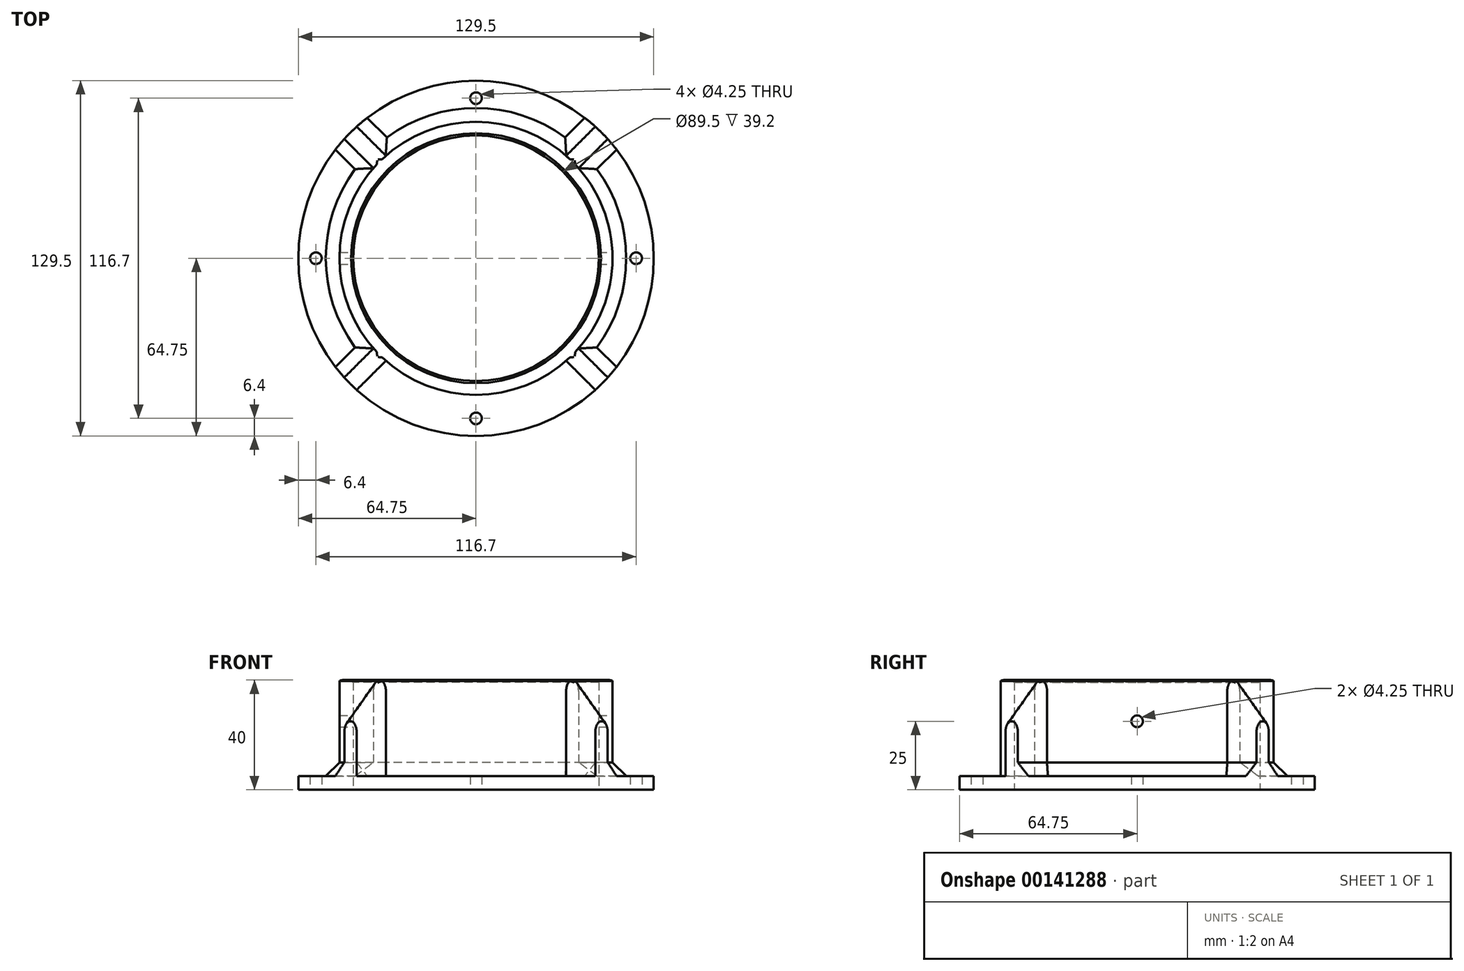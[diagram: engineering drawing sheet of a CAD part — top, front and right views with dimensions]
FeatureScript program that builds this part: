
annotation { "Feature Type Name" : "Feature", "Feature Type Description" : "" }
export const myFeature = defineFeature(function(context is Context, id is Id, definition is map)
    precondition{}
    {
        {
            var Q0;
            Q0=qCreatedBy(makeId("Top.planeOp"),FACE);
            var sketch = newSketch(context, id + "F0", { "sketchPlane" : qUnion([Q0])});
            skCircle(sketch, "E0", {"center": v(0, 0) * mm, "radius": 44.75 * mm});
            skCircle(sketch, "E1", {"center": v(0, 0) * mm, "radius": 64.75 * mm});
            skCircle(sketch, "E2", {"center": v(58.35, 0) * mm, "radius": 2.12 * mm});
            skCircle(sketch, "E3.1.0", {"center": v(0, 58.35) * mm, "radius": 2.12 * mm});
            skCircle(sketch, "E3.2.0", {"center": v(-58.35, 0) * mm, "radius": 2.12 * mm});
            skCircle(sketch, "E3.3.0", {"center": v(0, -58.35) * mm, "radius": 2.12 * mm});
            skSolve(sketch);
        }
        {
            var Q0;
            Q0=qSketchRegion(id+"F0",true);
            extrude(context, id + "F1", {"entities" : qUnion([Q0]), "depth" : 5 * mm});
        }
        {
            var Q0;
            Q0=makeQuery(id+"F1.opExtrude","CAP_FACE",FACE,{"disambiguationData":[OSD([sQuery(id+"F0.wireOp",EDGE,"E0"),sQuery(id+"F0.wireOp",EDGE,"E1")])],"isStart":false});
            var sketch = newSketch(context, id + "F2", { "sketchPlane" : qUnion([Q0])});
            skArc(sketch, "E4", {"start": v(-37.37, 32.84) * mm, "mid": v(-49.75, 0) * mm, "end": v(-37.37, -32.84) * mm});
            skCircle(sketch, "E5", {"center": v(0, 0) * mm, "radius": 44.75 * mm});
            skLineSegment(sketch, "E6", {"start": v(0, 0) * mm, "end": v(45.79, 45.79) * mm, "construction": true});
            skArc(sketch, "E7", {"start": v(43.47, 48) * mm, "mid": v(44.64, 46.9) * mm, "end": v(45.79, 45.79) * mm});
            skLineSegment(sketch, "E8", {"start": v(32.84, 37.37) * mm, "end": v(43.47, 48) * mm});
            skArc(sketch, "E9.MirrorCS", {"start": v(48, 43.47) * mm, "mid": v(46.9, 44.64) * mm, "end": v(45.79, 45.79) * mm});
            skLineSegment(sketch, "E10.MirrorCS", {"start": v(37.37, 32.84) * mm, "end": v(48, 43.47) * mm});
            skLineSegment(sketch, "E11.1.0", {"start": v(-37.37, 32.84) * mm, "end": v(-48, 43.47) * mm});
            skArc(sketch, "E11.1.1", {"start": v(-48, 43.47) * mm, "mid": v(-46.9, 44.64) * mm, "end": v(-45.79, 45.79) * mm});
            skArc(sketch, "E11.1.2", {"start": v(-43.47, 48) * mm, "mid": v(-44.64, 46.9) * mm, "end": v(-45.79, 45.79) * mm});
            skLineSegment(sketch, "E11.1.3", {"start": v(-32.84, 37.37) * mm, "end": v(-43.47, 48) * mm});
            skLineSegment(sketch, "E11.2.0", {"start": v(-32.84, -37.37) * mm, "end": v(-43.47, -48) * mm});
            skArc(sketch, "E11.2.1", {"start": v(-43.47, -48) * mm, "mid": v(-44.64, -46.9) * mm, "end": v(-45.79, -45.79) * mm});
            skArc(sketch, "E11.2.2", {"start": v(-48, -43.47) * mm, "mid": v(-46.9, -44.64) * mm, "end": v(-45.79, -45.79) * mm});
            skLineSegment(sketch, "E11.2.3", {"start": v(-37.37, -32.84) * mm, "end": v(-48, -43.47) * mm});
            skLineSegment(sketch, "E11.3.0", {"start": v(37.37, -32.84) * mm, "end": v(48, -43.47) * mm});
            skArc(sketch, "E11.3.1", {"start": v(48, -43.47) * mm, "mid": v(46.9, -44.64) * mm, "end": v(45.79, -45.79) * mm});
            skArc(sketch, "E11.3.2", {"start": v(43.47, -48) * mm, "mid": v(44.64, -46.9) * mm, "end": v(45.79, -45.79) * mm});
            skLineSegment(sketch, "E11.3.3", {"start": v(32.84, -37.37) * mm, "end": v(43.47, -48) * mm});
            skArc(sketch, "E12.trimOffspring", {"start": v(-32.84, -37.37) * mm, "mid": v(0, -49.75) * mm, "end": v(32.84, -37.37) * mm});
            skArc(sketch, "E13.trimOffspring", {"start": v(32.84, 37.37) * mm, "mid": v(0, 49.75) * mm, "end": v(-32.84, 37.37) * mm});
            skArc(sketch, "E14.trimOffspring", {"start": v(37.37, -32.84) * mm, "mid": v(49.75, 0) * mm, "end": v(37.37, 32.84) * mm});
            skSolve(sketch);
        }
        {
            var Q0;
            Q0=qSketchRegion(id+"F2",true);
            extrude(context, id + "F3", {"entities" : qUnion([Q0]), "operationType" : NewBodyOperationType.ADD, "depth" : 35 * mm});
        }
        {
            var Q0;
            Q0=makeQuery(id+"F3.opExtrude","CAP_EDGE",EDGE,{"disambiguationData":[OSD([sQuery(id+"F2.wireOp",EDGE,"E11.2.1"),sQuery(id+"F2.wireOp",EDGE,"E11.2.2")])],"isStart":false});
            var Q1;
            Q1=makeQuery(id+"F3.opExtrude","CAP_EDGE",EDGE,{"disambiguationData":[OSD([sQuery(id+"F2.wireOp",EDGE,"E11.3.1"),sQuery(id+"F2.wireOp",EDGE,"E11.3.2")])],"isStart":false});
            var Q2;
            Q2=makeQuery(id+"F3.opExtrude","CAP_EDGE",EDGE,{"disambiguationData":[OSD([sQuery(id+"F2.wireOp",EDGE,"E7"),sQuery(id+"F2.wireOp",EDGE,"E9.MirrorCS")])],"isStart":false});
            var Q3;
            Q3=makeQuery(id+"F3.opExtrude","CAP_EDGE",EDGE,{"disambiguationData":[OSD([sQuery(id+"F2.wireOp",EDGE,"E11.1.1"),sQuery(id+"F2.wireOp",EDGE,"E11.1.2")])],"isStart":false});
            chamfer(context, id + "F4", {"entities" : qUnion([Q0, Q1, Q2, Q3]), "width" : 15 * mm, "tangentPropagation" : true});
        }
        {
            var Q0;
            Q0=makeQuery(id+"F3.opExtrude","CAP_EDGE",EDGE,{"disambiguationData":[OSD([sQuery(id+"F2.wireOp",EDGE,"E12.trimOffspring")])],"isStart":true});
            var Q1;
            Q1=makeQuery(id+"F3.opExtrude","CAP_EDGE",EDGE,{"disambiguationData":[OSD([sQuery(id+"F2.wireOp",EDGE,"E11.3.3")])],"isStart":true});
            var Q2;
            Q2=makeQuery(id+"F3.opExtrude","CAP_EDGE",EDGE,{"disambiguationData":[OSD([sQuery(id+"F2.wireOp",EDGE,"E11.2.0")])],"isStart":true});
            var Q3;
            Q3=makeQuery(id+"F3.opExtrude","CAP_EDGE",EDGE,{"disambiguationData":[OSD([sQuery(id+"F2.wireOp",EDGE,"E14.trimOffspring")])],"isStart":true});
            var Q4;
            Q4=makeQuery(id+"F3.opExtrude","CAP_EDGE",EDGE,{"disambiguationData":[OSD([sQuery(id+"F2.wireOp",EDGE,"E10.MirrorCS")])],"isStart":true});
            var Q5;
            Q5=makeQuery(id+"F3.opExtrude","CAP_EDGE",EDGE,{"disambiguationData":[OSD([sQuery(id+"F2.wireOp",EDGE,"E11.3.0")])],"isStart":true});
            var Q6;
            Q6=makeQuery(id+"F3.opExtrude","CAP_EDGE",EDGE,{"disambiguationData":[OSD([sQuery(id+"F2.wireOp",EDGE,"E13.trimOffspring")])],"isStart":true});
            var Q7;
            Q7=makeQuery(id+"F3.opExtrude","CAP_EDGE",EDGE,{"disambiguationData":[OSD([sQuery(id+"F2.wireOp",EDGE,"E11.1.3")])],"isStart":true});
            var Q8;
            Q8=makeQuery(id+"F3.opExtrude","CAP_EDGE",EDGE,{"disambiguationData":[OSD([sQuery(id+"F2.wireOp",EDGE,"E8")])],"isStart":true});
            var Q9;
            Q9=makeQuery(id+"F3.opExtrude","CAP_EDGE",EDGE,{"disambiguationData":[OSD([sQuery(id+"F2.wireOp",EDGE,"E4")])],"isStart":true});
            var Q10;
            Q10=makeQuery(id+"F3.opExtrude","CAP_EDGE",EDGE,{"disambiguationData":[OSD([sQuery(id+"F2.wireOp",EDGE,"E11.1.0")])],"isStart":true});
            var Q11;
            Q11=makeQuery(id+"F3.opExtrude","CAP_EDGE",EDGE,{"disambiguationData":[OSD([sQuery(id+"F2.wireOp",EDGE,"E11.2.3")])],"isStart":true});
            chamfer(context, id + "F5", {"entities" : qUnion([Q0, Q1, Q2, Q3, Q4, Q5, Q6, Q7, Q8, Q9, Q10, Q11]), "width" : 5 * mm, "tangentPropagation" : true});
        }
        {
            var Q0;
            Q0=makeQuery(id+"F4.opChamfer","BLEND_EDGE",EDGE,{"blendedFrom":[makeQuery(id+"F3.opExtrude","CAP_EDGE",EDGE,{"disambiguationData":[OSD([sQuery(id+"F2.wireOp",EDGE,"E11.2.1"),sQuery(id+"F2.wireOp",EDGE,"E11.2.2")])],"isStart":false}),makeQuery(id+"F3.opExtrude","SWEPT_FACE",FACE,{"disambiguationData":[OSD([sQuery(id+"F2.wireOp",EDGE,"E11.2.3")])]})],"blendedInto":[makeQuery(id+"F3.opExtrude","SWEPT_FACE",FACE,{"disambiguationData":[OSD([sQuery(id+"F2.wireOp",EDGE,"E11.2.3")])]})]});
            var Q1;
            Q1=makeQuery(id+"F4.opChamfer","BLEND_EDGE",EDGE,{"blendedFrom":[makeQuery(id+"F3.opExtrude","CAP_EDGE",EDGE,{"disambiguationData":[OSD([sQuery(id+"F2.wireOp",EDGE,"E11.2.1"),sQuery(id+"F2.wireOp",EDGE,"E11.2.2")])],"isStart":false}),makeQuery(id+"F3.opExtrude","SWEPT_FACE",FACE,{"disambiguationData":[OSD([sQuery(id+"F2.wireOp",EDGE,"E11.2.0")])]})],"blendedInto":[makeQuery(id+"F3.opExtrude","SWEPT_FACE",FACE,{"disambiguationData":[OSD([sQuery(id+"F2.wireOp",EDGE,"E11.2.0")])]})]});
            var Q2;
            Q2=makeQuery(id+"F4.opChamfer","BLEND_EDGE",EDGE,{"blendedFrom":[makeQuery(id+"F3.opExtrude","CAP_EDGE",EDGE,{"disambiguationData":[OSD([sQuery(id+"F2.wireOp",EDGE,"E11.3.1"),sQuery(id+"F2.wireOp",EDGE,"E11.3.2")])],"isStart":false}),makeQuery(id+"F3.opExtrude","SWEPT_FACE",FACE,{"disambiguationData":[OSD([sQuery(id+"F2.wireOp",EDGE,"E11.3.3")])]})],"blendedInto":[makeQuery(id+"F3.opExtrude","SWEPT_FACE",FACE,{"disambiguationData":[OSD([sQuery(id+"F2.wireOp",EDGE,"E11.3.3")])]})]});
            var Q3;
            Q3=makeQuery(id+"F4.opChamfer","BLEND_EDGE",EDGE,{"blendedFrom":[makeQuery(id+"F3.opExtrude","CAP_EDGE",EDGE,{"disambiguationData":[OSD([sQuery(id+"F2.wireOp",EDGE,"E11.3.1"),sQuery(id+"F2.wireOp",EDGE,"E11.3.2")])],"isStart":false}),makeQuery(id+"F3.opExtrude","SWEPT_FACE",FACE,{"disambiguationData":[OSD([sQuery(id+"F2.wireOp",EDGE,"E11.3.0")])]})],"blendedInto":[makeQuery(id+"F3.opExtrude","SWEPT_FACE",FACE,{"disambiguationData":[OSD([sQuery(id+"F2.wireOp",EDGE,"E11.3.0")])]})]});
            var Q4;
            Q4=makeQuery(id+"F4.opChamfer","BLEND_EDGE",EDGE,{"blendedFrom":[makeQuery(id+"F3.opExtrude","CAP_EDGE",EDGE,{"disambiguationData":[OSD([sQuery(id+"F2.wireOp",EDGE,"E7"),sQuery(id+"F2.wireOp",EDGE,"E9.MirrorCS")])],"isStart":false}),makeQuery(id+"F3.opExtrude","SWEPT_FACE",FACE,{"disambiguationData":[OSD([sQuery(id+"F2.wireOp",EDGE,"E10.MirrorCS")])]})],"blendedInto":[makeQuery(id+"F3.opExtrude","SWEPT_FACE",FACE,{"disambiguationData":[OSD([sQuery(id+"F2.wireOp",EDGE,"E10.MirrorCS")])]})]});
            var Q5;
            Q5=makeQuery(id+"F4.opChamfer","BLEND_EDGE",EDGE,{"blendedFrom":[makeQuery(id+"F3.opExtrude","CAP_EDGE",EDGE,{"disambiguationData":[OSD([sQuery(id+"F2.wireOp",EDGE,"E7"),sQuery(id+"F2.wireOp",EDGE,"E9.MirrorCS")])],"isStart":false}),makeQuery(id+"F3.opExtrude","SWEPT_FACE",FACE,{"disambiguationData":[OSD([sQuery(id+"F2.wireOp",EDGE,"E8")])]})],"blendedInto":[makeQuery(id+"F3.opExtrude","SWEPT_FACE",FACE,{"disambiguationData":[OSD([sQuery(id+"F2.wireOp",EDGE,"E8")])]})]});
            var Q6;
            Q6=makeQuery(id+"F4.opChamfer","BLEND_EDGE",EDGE,{"blendedFrom":[makeQuery(id+"F3.opExtrude","CAP_EDGE",EDGE,{"disambiguationData":[OSD([sQuery(id+"F2.wireOp",EDGE,"E11.1.1"),sQuery(id+"F2.wireOp",EDGE,"E11.1.2")])],"isStart":false}),makeQuery(id+"F3.opExtrude","SWEPT_FACE",FACE,{"disambiguationData":[OSD([sQuery(id+"F2.wireOp",EDGE,"E11.1.3")])]})],"blendedInto":[makeQuery(id+"F3.opExtrude","SWEPT_FACE",FACE,{"disambiguationData":[OSD([sQuery(id+"F2.wireOp",EDGE,"E11.1.3")])]})]});
            var Q7;
            Q7=makeQuery(id+"F4.opChamfer","BLEND_EDGE",EDGE,{"blendedFrom":[makeQuery(id+"F3.opExtrude","CAP_EDGE",EDGE,{"disambiguationData":[OSD([sQuery(id+"F2.wireOp",EDGE,"E11.1.1"),sQuery(id+"F2.wireOp",EDGE,"E11.1.2")])],"isStart":false}),makeQuery(id+"F3.opExtrude","SWEPT_FACE",FACE,{"disambiguationData":[OSD([sQuery(id+"F2.wireOp",EDGE,"E11.1.0")])]})],"blendedInto":[makeQuery(id+"F3.opExtrude","SWEPT_FACE",FACE,{"disambiguationData":[OSD([sQuery(id+"F2.wireOp",EDGE,"E11.1.0")])]})]});
            fillet(context, id + "F6", {"entities" : qUnion([Q0, Q1, Q2, Q3, Q4, Q5, Q6, Q7]), "radius" : 3 * mm, "tangentPropagation" : true, "allowEdgeOverflow" : false});
        }
        {
            var Q0;
            Q0=makeQuery(id+"F3.opExtrude","CAP_EDGE",EDGE,{"disambiguationData":[OSD([sQuery(id+"F2.wireOp",EDGE,"E12.trimOffspring")])],"isStart":false});
            var Q1;
            Q1=makeQuery(id+"F3.opExtrude","CAP_EDGE",EDGE,{"disambiguationData":[OSD([sQuery(id+"F2.wireOp",EDGE,"E14.trimOffspring")])],"isStart":false});
            var Q2;
            Q2=makeQuery(id+"F3.opExtrude","CAP_EDGE",EDGE,{"disambiguationData":[OSD([sQuery(id+"F2.wireOp",EDGE,"E13.trimOffspring")])],"isStart":false});
            var Q3;
            Q3=makeQuery(id+"F3.opExtrude","CAP_EDGE",EDGE,{"disambiguationData":[OSD([sQuery(id+"F2.wireOp",EDGE,"E4")])],"isStart":false});
            fillet(context, id + "F7", {"entities" : qUnion([Q0, Q1, Q2, Q3]), "radius" : 3.2 * mm, "tangentPropagation" : true, "allowEdgeOverflow" : false});
        }
        {
            var Q0;
            Q0=qCreatedBy(makeId("Right.planeOp"),FACE);
            var sketch = newSketch(context, id + "F8", { "sketchPlane" : qUnion([Q0])});
            skCircle(sketch, "E15", {"center": v(0, 30) * mm, "radius": 2.25 * mm});
            skSolve(sketch);
        }
        {
            var Q0;
            Q0=qSketchRegion(id+"F8",true);
            extrude(context, id + "F9", {"entities" : qUnion([Q0]), "operationType" : NewBodyOperationType.REMOVE, "endBound" : BoundingType.SYMMETRIC, "oppositeDirection" : true, "depth" : 35 * mm});
        }
        {
            var Q0;
            Q0=qCreatedBy(makeId("Right.planeOp"),FACE);
            var sketch = newSketch(context, id + "F10", { "sketchPlane" : qUnion([Q0])});
            skCircle(sketch, "E16", {"center": v(0, 25) * mm, "radius": 2.13 * mm});
            skSolve(sketch);
        }
        {
            var Q0;
            Q0 = qSketchRegion(id + "F10", true);
            extrude(context, id + "F11", {"entities" : qUnion([Q0]), "operationType" : NewBodyOperationType.REMOVE, "endBound" : BoundingType.SYMMETRIC, "oppositeDirection" : true, "depth" : 100 * mm});
        }
        {
            var Q0;
            Q0=makeQuery(id+"F3.opExtrude","CAP_EDGE",EDGE,{"disambiguationData":[OSD([sQuery(id+"F2.wireOp",EDGE,"E5")])],"isStart":false});
            chamfer(context, id + "F12", {"entities" : qUnion([Q0]), "width" : .8 * mm, "tangentPropagation" : true});
        }
    });
